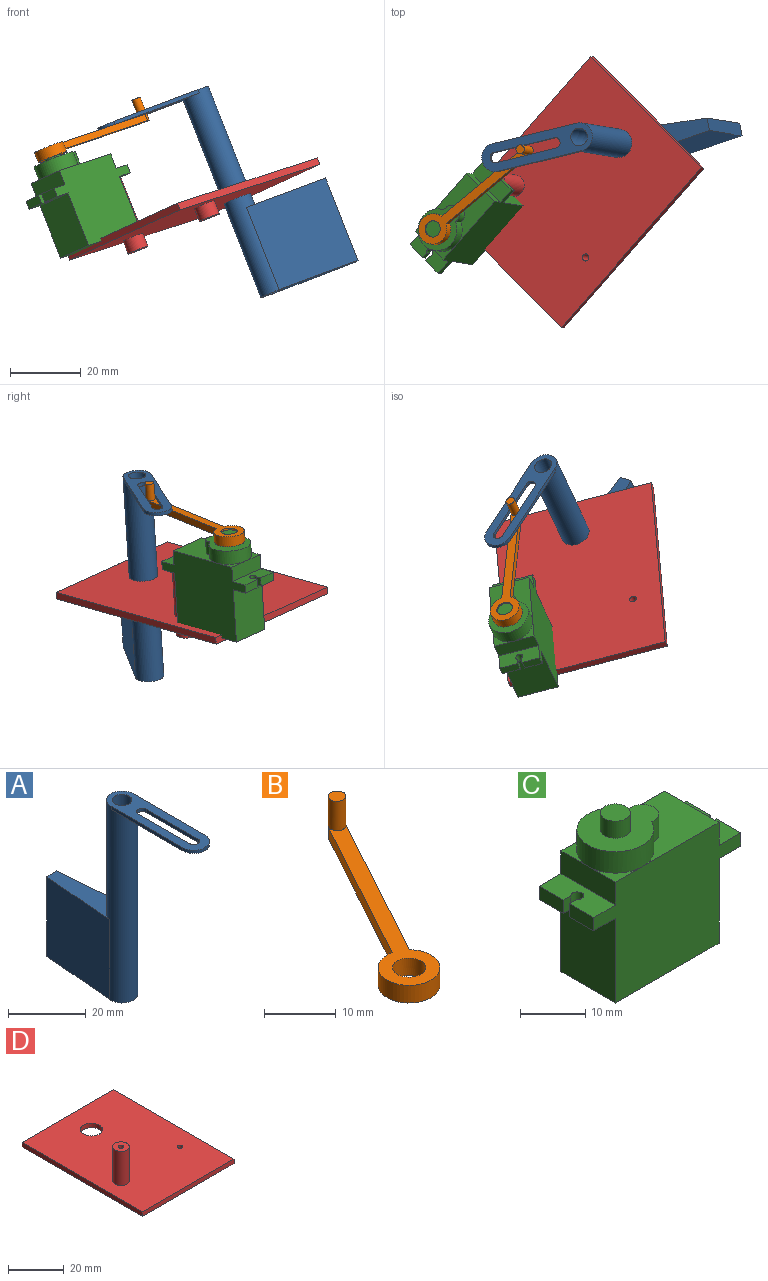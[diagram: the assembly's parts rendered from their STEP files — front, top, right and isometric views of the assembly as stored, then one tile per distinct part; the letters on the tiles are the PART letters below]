
ASSEMBLY  parts=4 mates=4
PART A: 16 faces, bbox 8x55.6x61 mm
  f0: cylinder r=4mm len=61mm, axis (0,0,-1), area 1240.6mm2, adj f4,f6,f9,f10,f11,f12,f14,f15
  f1: cylinder r=1.5mm len=3mm, axis (0,0,-1), area 4.7mm2, adj f2,f8,f9,f10
  f2: plane 18.59x1mm, normal (-1,0,0), area 18.6mm2, adj f1,f3,f9,f10
  f3: cylinder r=1.5mm len=3mm, axis (0,0,-1), area 4.7mm2, adj f2,f8,f9,f10
  f4: plane 26x1mm, normal (-1,0,0), area 26mm2, adj f0,f5,f9,f10
  f5: cylinder r=4mm len=8mm, axis (0,0,-1), area 12.6mm2, adj f4,f6,f9,f10
  f6: plane 26x1mm, normal (1,0,0), area 26mm2, adj f0,f5,f9,f10
  f7: cylinder r=2.5mm len=61mm, axis (0,0,-1), area 958.2mm2, adj f9,f11
  f8: plane 18.59x1mm, normal (1,0,0), area 18.6mm2, adj f1,f3,f9,f10
  f9: plane 34x8mm, normal (0,0,1), area 175.8mm2, adj f0,f1,f2,f3,f4,f5,f6,f7
  f10: plane 30x8mm, normal (0,0,-1), area 145.2mm2, adj f0,f1,f2,f3,f4,f5,f6,f8
  f11: plane 29.56x8mm, normal (0,0,-1), area 154mm2, adj f0,f7,f12,f13,f14
  f12: plane 25x24.88mm, normal (-1,0.09,0), area 624.3mm2, adj f0,f11,f13,f15
  f13: plane 25x3.62mm, normal (0,1,0), area 90.4mm2, adj f11,f12,f14,f15
  f14: plane 25x24.88mm, normal (1,0.09,0), area 624.3mm2, adj f0,f11,f13,f15
  f15: plane 24.88x7.88mm, normal (0,0,1), area 123.3mm2, adj f0,f12,f13,f14
PART B: 9 faces, bbox 22.7x36.8x8 mm
  f0: plane 29.54x17.49mm, normal (0,0,-1), area 81mm2, adj f1,f2,f3,f6
  f1: plane 27.69x15.14mm, normal (0.88,-0.48,0), area 63.1mm2, adj f0,f2,f4,f6
  f2: cylinder r=1.25mm len=7mm, axis (0,0,1), area 47.1mm2, adj f0,f1,f3,f4,f5
  f3: plane 27.69x15.14mm, normal (-0.88,0.48,0), area 63.1mm2, adj f0,f2,f4,f6
  f4: plane 36.2x22.51mm, normal (0,0,1), area 117.6mm2, adj f1,f2,f3,f6,f7
  f5: plane 2.5x2.5mm, normal (0,0,1), area 4.9mm2, adj f2
  f6: cylinder r=4.3mm len=8.6mm, axis (0,0,-1), area 76mm2, adj f0,f1,f3,f4,f8
  f7: cylinder r=2.3mm len=4.6mm, axis (0,0,-1), area 43.4mm2, adj f4,f8
  f8: plane 8.6x8.6mm, normal (0,0,-1), area 41.5mm2, adj f6,f7
PART C: 29 faces, bbox 31.9x11.8x29.9 mm
  f0: plane 5.25x2.5mm, normal (1,0,0), area 13.1mm2, adj f6,f10,f13,f26
  f1: plane 5.25x2.5mm, normal (-1,0,0), area 13.1mm2, adj f4,f6,f14,f25
  f2: plane 16.6x11.8mm, normal (0,0,1), area 130.5mm2, adj f6,f8,f16,f18,f19
  f3: plane 5.9x5.9mm, normal (0,0,1), area 7.5mm2, adj f8,f15,f19
  f4: plane 11.8x4.7mm, normal (0,0,1), area 50.5mm2, adj f1,f6,f8,f12,f15,f23,f24,f25
  f5: plane 15.9x11.8mm, normal (-1,0,0), area 187.6mm2, adj f6,f8,f9,f14
  f6: plane 31.9x22.7mm, normal (0,-1,0), area 534.2mm2, adj f0,f1,f2,f4,f5,f7,f9,f10
  f7: plane 15.9x11.8mm, normal (1,0,0), area 187.6mm2, adj f6,f8,f9,f10
  f8: plane 31.9x22.7mm, normal (0,1,0), area 534.2mm2, adj f2,f3,f4,f5,f7,f9,f10,f11
  f9: plane 22.5x11.8mm, normal (0,0,-1), area 265.5mm2, adj f5,f6,f7,f8
  f10: plane 11.8x4.7mm, normal (0,0,-1), area 50.5mm2, adj f0,f6,f7,f8,f11,f26,f27,f28
  f11: plane 5.25x2.5mm, normal (1,0,0), area 13.1mm2, adj f8,f10,f13,f27
  f12: plane 5.25x2.5mm, normal (-1,0,0), area 13.1mm2, adj f4,f8,f14,f24
  f13: plane 11.8x4.7mm, normal (0,0,1), area 50.5mm2, adj f0,f6,f8,f11,f16,f26,f27,f28
  f14: plane 11.8x4.7mm, normal (0,0,-1), area 50.5mm2, adj f1,f5,f6,f8,f12,f23,f24,f25
  f15: plane 11.8x4.3mm, normal (-1,0,0), area 50.7mm2, adj f3,f4,f6,f8,f17
  f16: plane 11.8x4.3mm, normal (1,0,0), area 50.7mm2, adj f2,f6,f8,f13
  f17: plane 5.9x5.9mm, normal (0,0,1), area 7.5mm2, adj f6,f15,f19
  f18: cylinder r=2.5mm len=5mm, axis (0,0,-1), area 35.7mm2, adj f2,f19,f20
  f19: cylinder r=5.9mm len=11.8mm, axis (0,0,-1), area 128.1mm2, adj f2,f3,f17,f18,f20
  f20: plane 14.3x11.8mm, normal (0,0,1), area 103.4mm2, adj f18,f19,f21
  f21: cylinder r=2.3mm len=4.6mm, axis (0,0,-1), area 46.2mm2, adj f20,f22
  f22: plane 4.6x4.6mm, normal (0,0,1), area 16.6mm2, adj f21
  f23: cylinder r=1mm len=2.5mm, axis (0,0,1), area 12.2mm2, adj f4,f14,f24,f25
  f24: plane 2.5x1.59mm, normal (0,-1,0), area 4mm2, adj f4,f12,f14,f23
  f25: plane 2.5x1.59mm, normal (0,1,0), area 4mm2, adj f1,f4,f14,f23
  f26: plane 2.5x1.59mm, normal (0,1,0), area 4mm2, adj f0,f10,f13,f28
  f27: plane 2.5x1.59mm, normal (0,-1,0), area 4mm2, adj f10,f11,f13,f28
  f28: cylinder r=1mm len=2.5mm, axis (0,0,1), area 12.2mm2, adj f10,f13,f26,f27
PART D: 15 faces, bbox 46.5x61.2x21 mm
  f0: plane 61.16x46.51mm, normal (0,0,-1), area 2737.8mm2, adj f1,f2,f3,f4,f5,f8,f10
  f1: plane 61.16x2mm, normal (-1,0,0), area 122.3mm2, adj f0,f2,f4,f6
  f2: plane 46.51x2mm, normal (0,-1,0), area 93mm2, adj f0,f1,f3,f6
  f3: plane 61.16x2mm, normal (1,0,0), area 122.3mm2, adj f0,f2,f4,f6
  f4: plane 46.51x2mm, normal (0,1,0), area 93mm2, adj f0,f1,f3,f6
  f5: cylinder r=4mm len=8mm, axis (0,0,-1), area 50.3mm2, adj f0,f6
  f6: plane 61.16x46.51mm, normal (0,0,1), area 2763mm2, adj f1,f2,f3,f4,f5,f11,f13
  f7: cylinder r=1mm len=21mm, axis (0,0,1), area 131.9mm2, adj f9,f14
  f8: cylinder r=3mm len=6mm, axis (0,0,1), area 75.4mm2, adj f0,f9
  f9: plane 6x6mm, normal (0,0,-1), area 25.1mm2, adj f7,f8
  f10: cylinder r=3mm len=6mm, axis (0,0,1), area 75.4mm2, adj f0,f12
  f11: cylinder r=1mm len=6mm, axis (0,0,1), area 37.7mm2, adj f6,f12
  f12: plane 6x6mm, normal (0,0,-1), area 25.1mm2, adj f10,f11
  f13: cylinder r=3mm len=15mm, axis (0,0,-1), area 282.7mm2, adj f6,f14
  f14: plane 6x6mm, normal (0,0,1), area 25.1mm2, adj f7,f13
PLACE A rot(axis=(0.15,-0.25,-0.96),80.3deg) t=(-36.35,-131.64,-62.04)mm
PLACE B rot(axis=(0.03,-0.68,-0.73),31.9deg) t=(-48.7,-128.53,-67.1)mm
PLACE C rot(axis=(-0.23,-0.37,0.9),51.3deg) t=(-66.73,-167.56,-104.5)mm
PLACE D rot(axis=(0.1,-0.45,-0.89),48.1deg) t=(-72.15,-153.88,-108.66)mm fixed
MATE cylindrical A.f0 <-> D.f5  axis (0.37,-0.06,-0.93) through (-25.56,-133.34,-89.45)mm
MATE fastened D.f7 <-> C.f28  axis (-0.37,0.06,0.93) through (-60.46,-144.39,-86.35)mm
MATE pin_slot B.f2 <-> A.f5  axis (-0.37,0.06,0.93) through (-51.53,-135.35,-67.79)mm
MATE cylindrical B.f6 <-> C.f19  axis (-0.37,0.06,0.93) through (-77.99,-157.49,-76.83)mm
